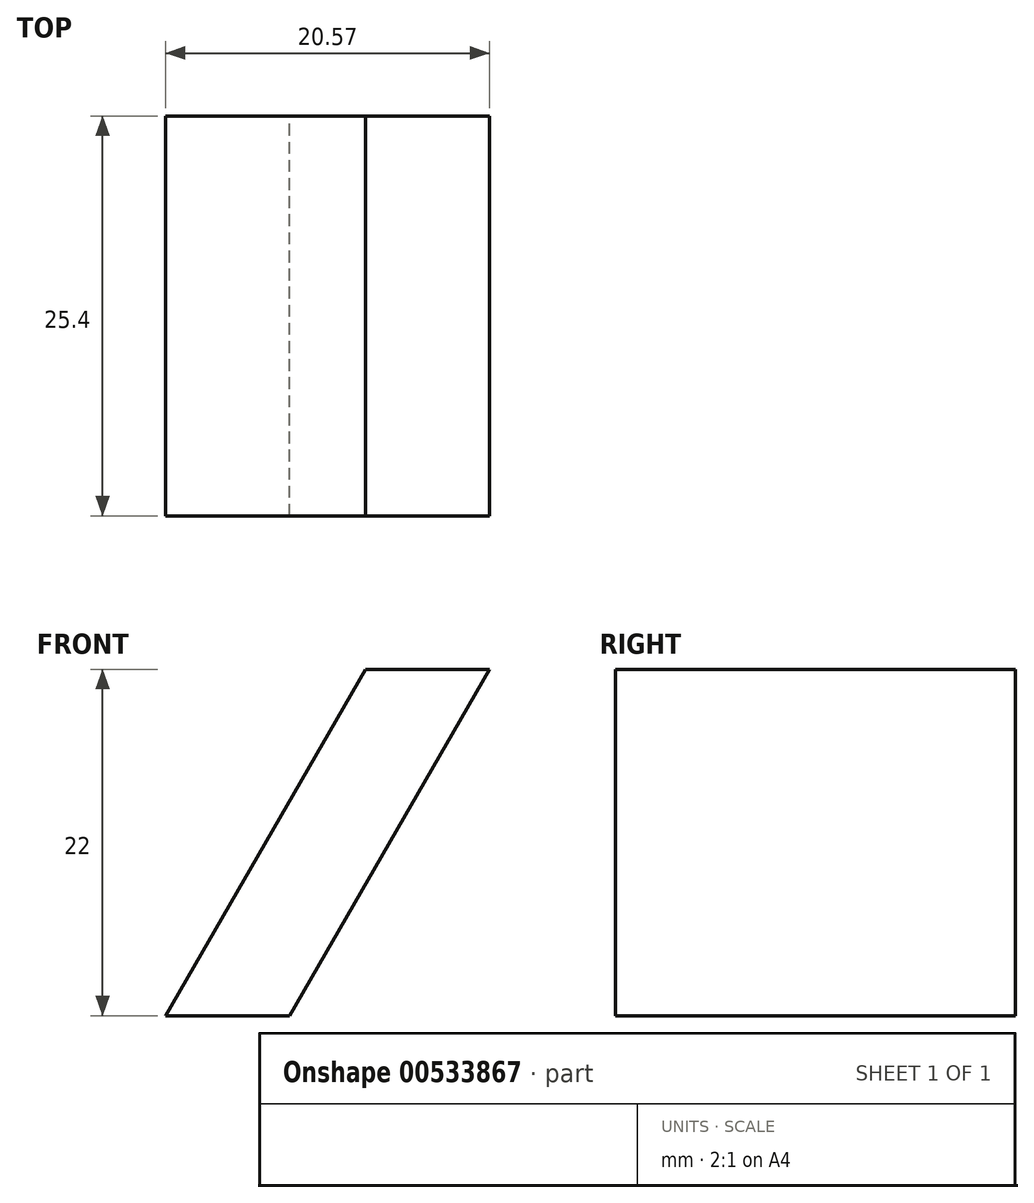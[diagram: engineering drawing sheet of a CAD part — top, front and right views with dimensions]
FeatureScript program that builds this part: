
annotation { "Feature Type Name" : "Feature", "Feature Type Description" : "" }
export const myFeature = defineFeature(function(context is Context, id is Id, definition is map)
    precondition{}
    {
        {
            var Q0;
            Q0=qCreatedBy(makeId("Front.planeOp"),FACE);
            var sketch = newSketch(context, id + "F0", { "sketchPlane" : qUnion([Q0])});
            skLineSegment(sketch, "E0", {"start": v(-12.9, -11.34) * mm, "end": v(-0.2, 10.66) * mm});
            skLineSegment(sketch, "E1", {"start": v(-0.2, 10.66) * mm, "end": v(7.67, 10.66) * mm});
            skLineSegment(sketch, "E2", {"start": v(7.67, 10.66) * mm, "end": v(-5.03, -11.34) * mm});
            skLineSegment(sketch, "E3", {"start": v(-12.9, -11.34) * mm, "end": v(-5.03, -11.34) * mm});
            skSolve(sketch);
        }
        {
            var Q0;
            Q0=makeQuery(id+"F0.imprint","IMPRINT",FACE,{"disambiguationData":[TD([[makeQuery(id+"F0.imprint","IMPRINT",EDGE,{"derivedFrom":sQuery(id+"F0.wireOp",EDGE,"E0")}),-1.0]])]});
            extrude(context, id + "F1", {"entities" : qUnion([Q0]), "depth" : 25.4 * mm, "offsetDistance" : 25.4 * mm});
        }
    });
